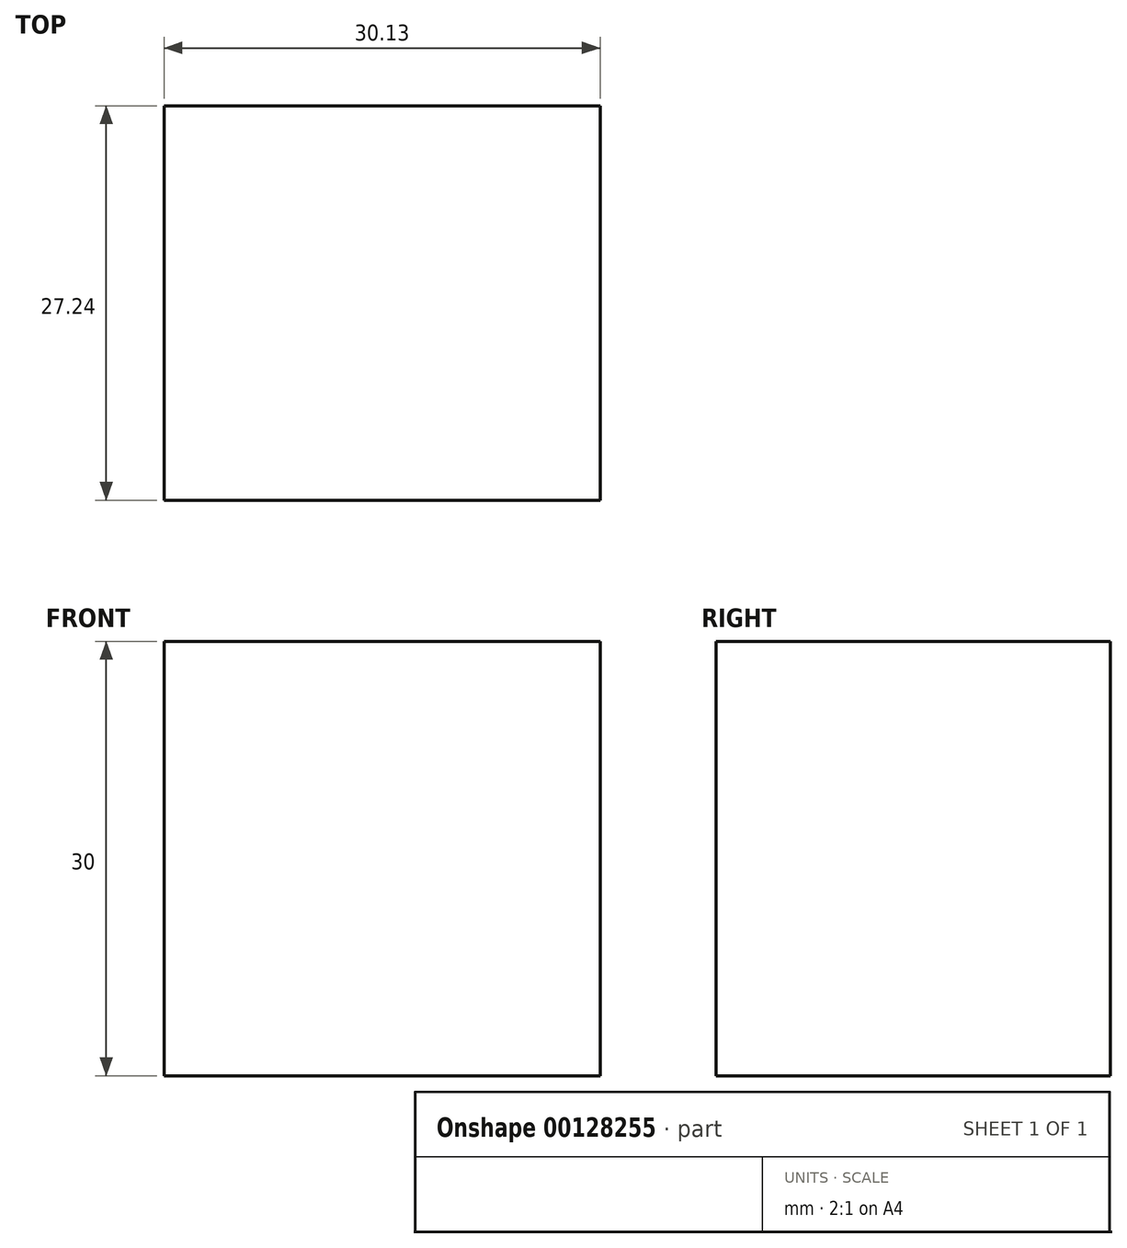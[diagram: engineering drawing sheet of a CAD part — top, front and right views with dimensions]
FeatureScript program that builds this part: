
annotation { "Feature Type Name" : "Feature", "Feature Type Description" : "" }
export const myFeature = defineFeature(function(context is Context, id is Id, definition is map)
    precondition{}
    {
        {
            var Q0;
            Q0=qCreatedBy(makeId("Top.planeOp"),FACE);
            var sketch = newSketch(context, id + "F0", { "sketchPlane" : qUnion([Q0])});
            skLineSegment(sketch, "E0", {"start": v(0, 0) * mm, "end": v(30.13, 0) * mm});
            skLineSegment(sketch, "E1", {"start": v(30.13, 0) * mm, "end": v(30.13, 27.24) * mm});
            skLineSegment(sketch, "E2", {"start": v(30.13, 27.24) * mm, "end": v(0, 27.24) * mm});
            skLineSegment(sketch, "E3", {"start": v(0, 27.24) * mm, "end": v(0, 0) * mm});
            skSolve(sketch);
        }
        {
            var Q0;
            Q0 = qSketchRegion(id + "F0", true);
            extrude(context, id + "F1", {"entities" : qUnion([Q0]), "depth" : 5 * mm});
        }
        {
            var Q0;
            Q0=makeQuery(id+"F1.opExtrude","CAP_FACE",FACE,{"disambiguationData":[OSD([sQuery(id+"F0.wireOp",EDGE,"E0"),sQuery(id+"F0.wireOp",EDGE,"E1"),sQuery(id+"F0.wireOp",EDGE,"E2"),sQuery(id+"F0.wireOp",EDGE,"E3")])],"isStart":false});
            var sketch = newSketch(context, id + "F2", { "sketchPlane" : qUnion([Q0])});
            skLineSegment(sketch, "E4", {"start": v(30.13, 0) * mm, "end": v(10.5, 0) * mm});
            skLineSegment(sketch, "E5", {"start": v(10.5, 0) * mm, "end": v(10.5, 9.16) * mm});
            skLineSegment(sketch, "E6", {"start": v(10.5, 9.16) * mm, "end": v(30.13, 9.16) * mm});
            skLineSegment(sketch, "E7", {"start": v(30.13, 9.16) * mm, "end": v(30.13, 0) * mm});
            skLineSegment(sketch, "E8", {"start": v(10.5, 9.16) * mm, "end": v(0, 9.16) * mm});
            skLineSegment(sketch, "E9", {"start": v(0, 9.16) * mm, "end": v(0, 0) * mm});
            skLineSegment(sketch, "E10", {"start": v(0, 0) * mm, "end": v(10.5, 0) * mm});
            skLineSegment(sketch, "E11", {"start": v(30.13, 9.16) * mm, "end": v(30.13, 27.24) * mm});
            skLineSegment(sketch, "E12", {"start": v(30.13, 27.24) * mm, "end": v(0, 27.24) * mm});
            skLineSegment(sketch, "E13", {"start": v(0, 27.24) * mm, "end": v(0, 9.16) * mm});
            skSolve(sketch);
        }
        {
            var Q0;
            Q0 = qSketchRegion(id + "F2", true);
            extrude(context, id + "F3", {"entities" : qUnion([Q0]), "operationType" : NewBodyOperationType.ADD, "depth" : 25 * mm});
        }
    });
